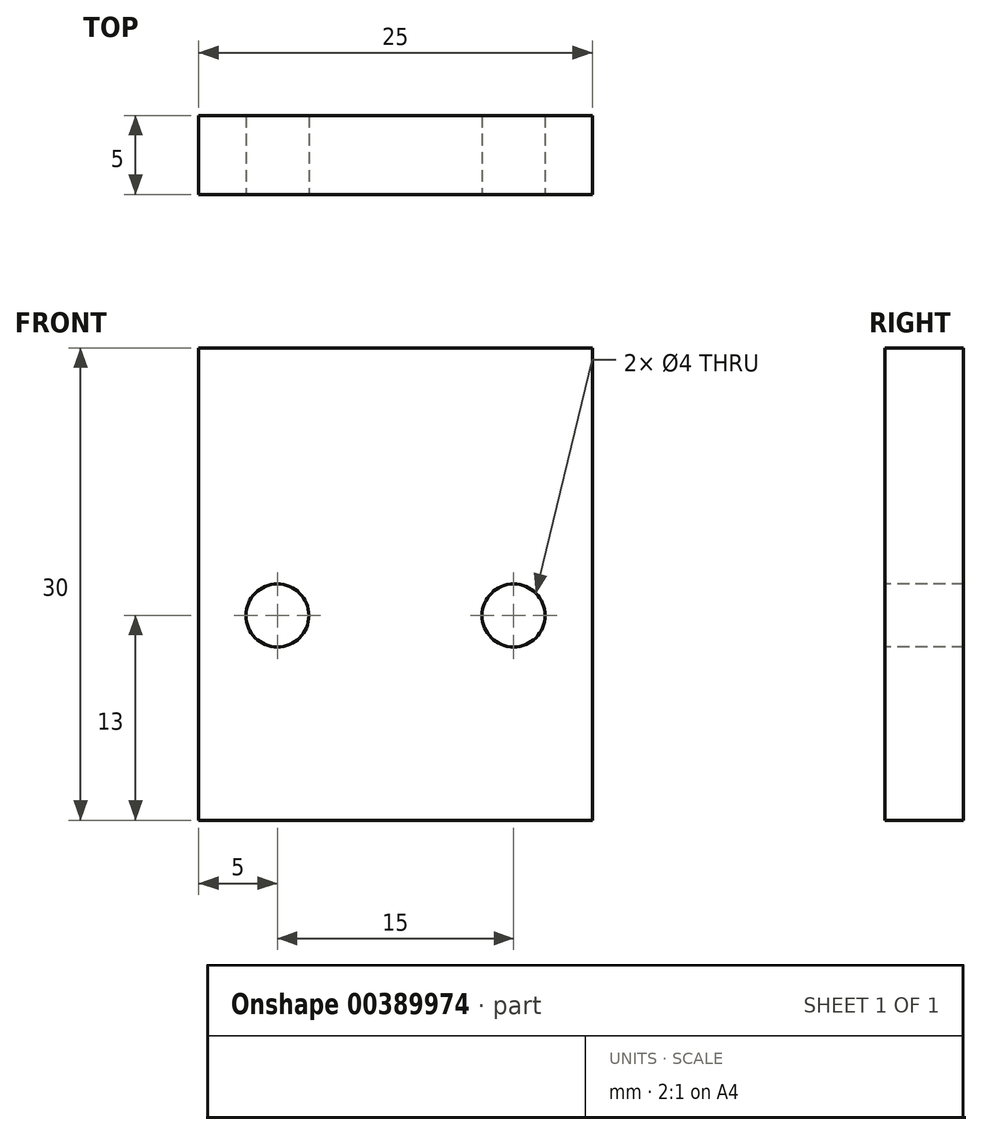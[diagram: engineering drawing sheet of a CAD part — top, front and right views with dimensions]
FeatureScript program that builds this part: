
annotation { "Feature Type Name" : "Feature", "Feature Type Description" : "" }
export const myFeature = defineFeature(function(context is Context, id is Id, definition is map)
    precondition{}
    {
        {
            var Q0;
            Q0=qCreatedBy(makeId("Front.planeOp"),FACE);
            var sketch = newSketch(context, id + "F0", { "sketchPlane" : qUnion([Q0])});
            skLineSegment(sketch, "E0.bottom", {"start": v(12.5, 15) * mm, "end": v(-12.5, 15) * mm});
            skLineSegment(sketch, "E0.top", {"start": v(12.5, -15) * mm, "end": v(-12.5, -15) * mm});
            skLineSegment(sketch, "E0.left", {"start": v(12.5, 15) * mm, "end": v(12.5, -15) * mm});
            skLineSegment(sketch, "E0.right", {"start": v(-12.5, 15) * mm, "end": v(-12.5, -15) * mm});
            skPoint(sketch, "E0.middle", {"position": v(0, 0) * mm});
            skLineSegment(sketch, "E1.bottom", {"start": v(25.6, 3) * mm, "end": v(-25.6, 3) * mm, "construction": true});
            skLineSegment(sketch, "E1.top", {"start": v(25.6, -7) * mm, "end": v(-25.6, -7) * mm, "construction": true});
            skLineSegment(sketch, "E1.left", {"start": v(25.6, 3) * mm, "end": v(25.6, -7) * mm, "construction": true});
            skLineSegment(sketch, "E1.right", {"start": v(-25.6, 3) * mm, "end": v(-25.6, -7) * mm, "construction": true});
            skPoint(sketch, "E1.middle", {"position": v(0, -2) * mm});
            skLineSegment(sketch, "E2", {"start": v(-7.5, -2) * mm, "end": v(7.5, -2) * mm, "construction": true});
            skCircle(sketch, "E3", {"center": v(7.5, -2) * mm, "radius": 2 * mm});
            skCircle(sketch, "E4", {"center": v(-7.5, -2) * mm, "radius": 2 * mm});
            skSolve(sketch);
        }
        {
            var Q0;
            Q0 = qSketchRegion(id + "F0", true);
            extrude(context, id + "F1", {"entities" : qUnion([Q0]), "oppositeDirection" : true, "depth" : 5 * mm});
        }
    });
